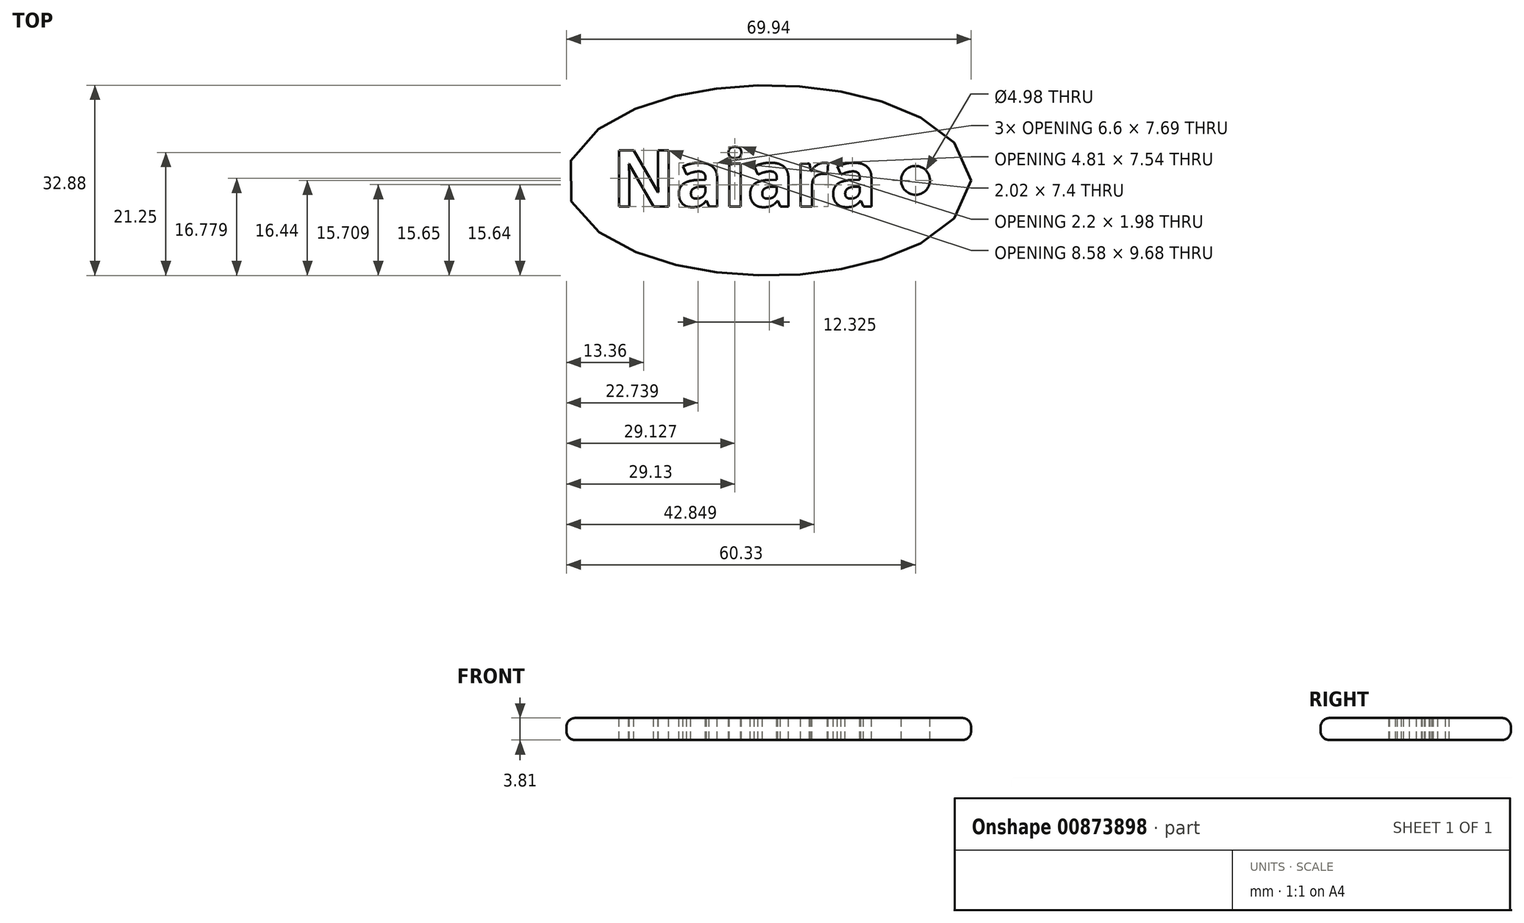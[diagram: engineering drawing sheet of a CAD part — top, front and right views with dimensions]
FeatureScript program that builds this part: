
annotation { "Feature Type Name" : "Feature", "Feature Type Description" : "" }
export const myFeature = defineFeature(function(context is Context, id is Id, definition is map)
    precondition{}
    {
        {
            var Q0;
            Q0=qCreatedBy(makeId("Top.planeOp"),FACE);
            var sketch = newSketch(context, id + "F0", { "sketchPlane" : qUnion([Q0])});
            skEllipse(sketch, "E0", {"center": v(0, 0) * mm, "majorRadius": 34.97 * mm, "minorRadius": 16.44 * mm, "majorAxis": v(1, 0)});
            skSolve(sketch);
        }
        {
            var Q0;
            Q0=qSketchRegion(id+"F0",true);
            extrude(context, id + "F1", {"entities" : qUnion([Q0]), "depth" : 3.8 * mm, "offsetDistance" : 25.4 * mm});
        }
        {
            var Q0;
            Q0=makeQuery(id+"F1.opExtrude","CAP_FACE",FACE,{"disambiguationData":[OSD([sQuery(id+"F0.wireOp",EDGE,"E0")])],"isStart":false});
            var Q1;
            Q1=makeQuery(id+"F1.opExtrude","CAP_FACE",FACE,{"disambiguationData":[OSD([sQuery(id+"F0.wireOp",EDGE,"E0")])],"isStart":true});
            fillet(context, id + "F2", {"entities" : qUnion([Q0, Q1]), "radius" : 1.52 * mm, "tangentPropagation" : true, "allowEdgeOverflow" : false});
        }
        {
            var Q0;
            Q0=makeQuery(id+"F1.opExtrude","CAP_FACE",FACE,{"disambiguationData":[OSD([sQuery(id+"F0.wireOp",EDGE,"E0")])],"isStart":false});
            var sketch = newSketch(context, id + "F3", { "sketchPlane" : qUnion([Q0])});
            skText(sketch, "E1", { "text": "Naiara", "fontName": "OpenSans-Bold.ttf"});
            skCircle(sketch, "E2", {"center": v(25.36, 0) * mm, "radius": 2.5 * mm});
            const initialGuessF3  = {"E1": [-0.02712, -0.0045, 1, 0, 0.00976]};
            skSetInitialGuess(sketch, initialGuessF3);
            skSolve(sketch);
        }
        {
            var Q0;
            Q0=qSketchRegion(id+"F3",true);
            extrude(context, id + "F4", {"entities" : qUnion([Q0]), "operationType" : NewBodyOperationType.REMOVE, "endBound" : BoundingType.THROUGH_ALL, "oppositeDirection" : true, "depth" : 25.4 * mm, "offsetDistance" : 25.4 * mm});
        }
    });
